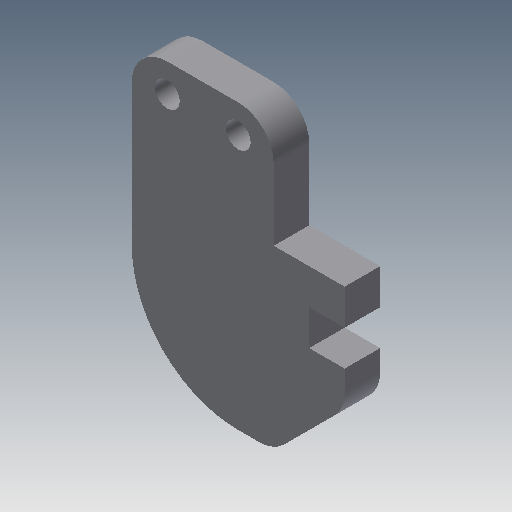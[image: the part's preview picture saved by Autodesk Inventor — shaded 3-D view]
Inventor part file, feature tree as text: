
AUTODESK INVENTOR PART (.ipt)
format: ipt  version: 2018 (Build 220112000, 112)  size: 123,392 bytes
history: native  units: mm
features: extrude x2, sketch x2
ambient origin geometry x8: Origin, YZ Plane, XZ Plane, XY Plane, X Axis, Y Axis, Z Axis, Center Point
bodies: Solid1 (feature_tree)
feature tree (4):
  extrude  "Extrusion1"  Depth=10.0mm
  extrude  "Extrusion2"  Depth=15.0mm
  sketch  "Sketch1"  dims[d0=10.0mm d1=10.0mm]
  sketch  "Sketch2"  dims[d2=20.0mm d3=15.0mm d4=10.0mm d5=5.0mm d6=5.0mm d7=5.0mm d8=135.0deg d9=5.0mm d10=15.0mm d11=5.0mm d12=5.0mm d13=0.0mm d14=6.0mm d15=5.0mm d16=10.0mm d17=3.5mm d18=3.5mm d19=5.0mm d20=0.0mm d21=5.0mm]
